# Revit family: PRD_FrankeWS_Shlvs_Heavy-DutyShelf_AL300HD,TA500HD,TA600HD
name_source: partatom
category: Furniture
revit_build: Autodesk Revit 2018 (Build: 20190510_1515(x64)
units: mm (PartAtom-declared; Revit-internal decimal feet)

## family parameters
Cut with Voids When Loaded = No
Host = Face
OmniClass Number = 23.40.20.00
OmniClass Title = General Furniture and Specialties
Room Calculation Point = No
Shared = No

## types (3) — shared parameters
AssetType = Fixed
Category = Pr_40_30_78_06, Bathroom shelves
Color = Stainless steel
Default Elevation = 1500 mm  [stored 4.92126 ft]
DurationUnit = year
Finish = Satin finished
FinishAndColour = Stainless steel 1.4301, satin finished
Form = Wall mounted
IfcExportAs = IfcFurnitureType
IfcExportType = NOTDEFINED
IntegralAccessories = Incl. stainless steel crosshead screws and dowels
MainColor = Stainless steel
Manufacturer = KWC Group AG
ManufacturerName = KWC Group AG
ManufacturerURL = www.kwc.com
Material = Stainless steel
NBSDescription = Shelves
NBSReference = 45-35-72/354
NominalDepth = 80 mm  [stored 0.262467 ft]
NominalHeight = 30 mm  [stored 0.0984252 ft]
ProductInformation = https://pim.kwc.com
Shape = Rectangular
ShelfMaterial = PRD_AR_StainlessSteel_SatinFinished
Style = Shelf
TypeOfMounting = Wall mounting
URL = www.kwc.com
Uniclass2015Code = Pr_40_30_78_06
Uniclass2015Title = Bathroom shelves
Uniclass2015Version = Products v1.10
Version = 1
WarrantyDurationUnit = year

## per-type parameters (varying)
| type | BIMObjectName | Description | Features | GrossWeight | ModelNumber | Name | NetWeight | NominalWidth | OverallWidth | Size |
| TA500HD | PRD_AR_Shelves_Heavy-DutyShelf_TA500HD | Shelf for wall mounting, stainless steel, surface satin finished, Material thickness 2 mm, rounded edges, protection edge at front. Incl. stainless steel crosshead screws and dowels. length 500 mm | stainless steel, 2.00 mm, satin finished, wall mounting, 500x30x80 mm (WxHxD) | 1.15 kg | 2000102702 | HEAVY-DUTY shelf TA500HD | 1.00 kg | 500 mm  [stored 1.64042 ft] | 500 mm  [stored 1.64042 ft] | 500 x 30 x 80 mm |
| AL300HD | PRD_AR_Shelves_Heavy-DutyShelf_AL300HD | Shelf for wall mounting, stainless steel, surface satin finished, Material thickness 2 mm, rounded edges, protection edge at front. Incl. stainless steel crosshead screws and dowels. length 300 mm | stainless steel, 2.00 mm, satin finished, wall mounting, 300x30x80 mm (WxHxD) | 0.80 kg | 2000056718 | HEAVY-DUTY shelf AL300HD | 0.60 kg | 300 mm  [stored 0.984252 ft] | 300 mm  [stored 0.984252 ft] | 300 x 30 x 80 mm |
| TA600HD | PRD_AR_Shelves_Heavy-DutyShelf_TA600HD | Shelf for wall mounting, stainless steel, surface satin finished, Material thickness 2 mm, rounded edges, protection edge at front. Incl. stainless steel crosshead screws and dowels. length 600 mm | stainless steel, 2.00 mm, satin finished, wall mounting, 600x30x80 mm (WxHxD) | 1.35 kg | 2000090054 | HEAVY-DUTY shelf TA600HD | 1.15 kg | 600 mm | 600 mm | 600 x 30 x 80 mm |

note: column(s) folded — value = type name in every type: Model, ModelReference

note: [stored X ft] marks values corroborated as IEEE doubles in the binary element streams (Revit-internal decimal feet)

## geometry (parser evidence)
native form markers: Sweep x2
no freeform markers — native parametric forms only
